# Revit family: P6829
name_source: partatom
category: Lighting Fixtures
revit_build: Autodesk Revit 2014 (Build: 20130308_1515(x64)
units: mm (PartAtom-declared; Revit-internal decimal feet)

## types (1)
- P6829
    Apparent Load = 5 VA
    Assembly Code = D5020200
    Color Filter = 16777215
    Connector Description = Lighting Connector
    Default Elevation = 48 "
    Depth = 0.875 "
    Description = The 5w, 3000K step light/wall lights is a horizontal mount that mounts in a single-gang wall box. 84+ CRI and 120 degree beam spread. Wet location listed so can be used indoor or outdoors. Brushed Nickel finish.
    Dimming Lamp Color Temperature Shift = <None>
    Features = Brushed Nickel finish.
Can be used indoor or outdoor
3000K color temperature 84+ CRI
65 lumens (delivered).
    Fixture distribution = Direct
    Glass = Hubbell - Glass
    HeightLength = 4.75 "
    Housing Material = Paint - Hubbell -nickel
    Lamp = LED
    Load Classification = Lighting
    Manufacturer = Progress Lighting
    Model = P6829
    Mounting = Paint - Hubbell - Light Silver
    Photometric Web File = PROG_P6832_15.00137 Series_testlabreports.ies
    Power Factor = 1
    Product Documentation Link = https://hubbellcdn.com
    Product Link = https://www.hubbell.com
    Reflector Finish = Hubbell - White Glass
    Tilt Angle = -120.00°
    URL = https://www.hubbell.com
    Voltage = 120 V
    Warranty = 5 years Warranty
    Wattage Comments = 4.5W
    Watts = 5 W
    Width = 3 "
    Wings = Paint - Hubbell - Light Silver

## geometry (parser evidence)
native form markers: Sweep x4
no freeform markers — native parametric forms only
